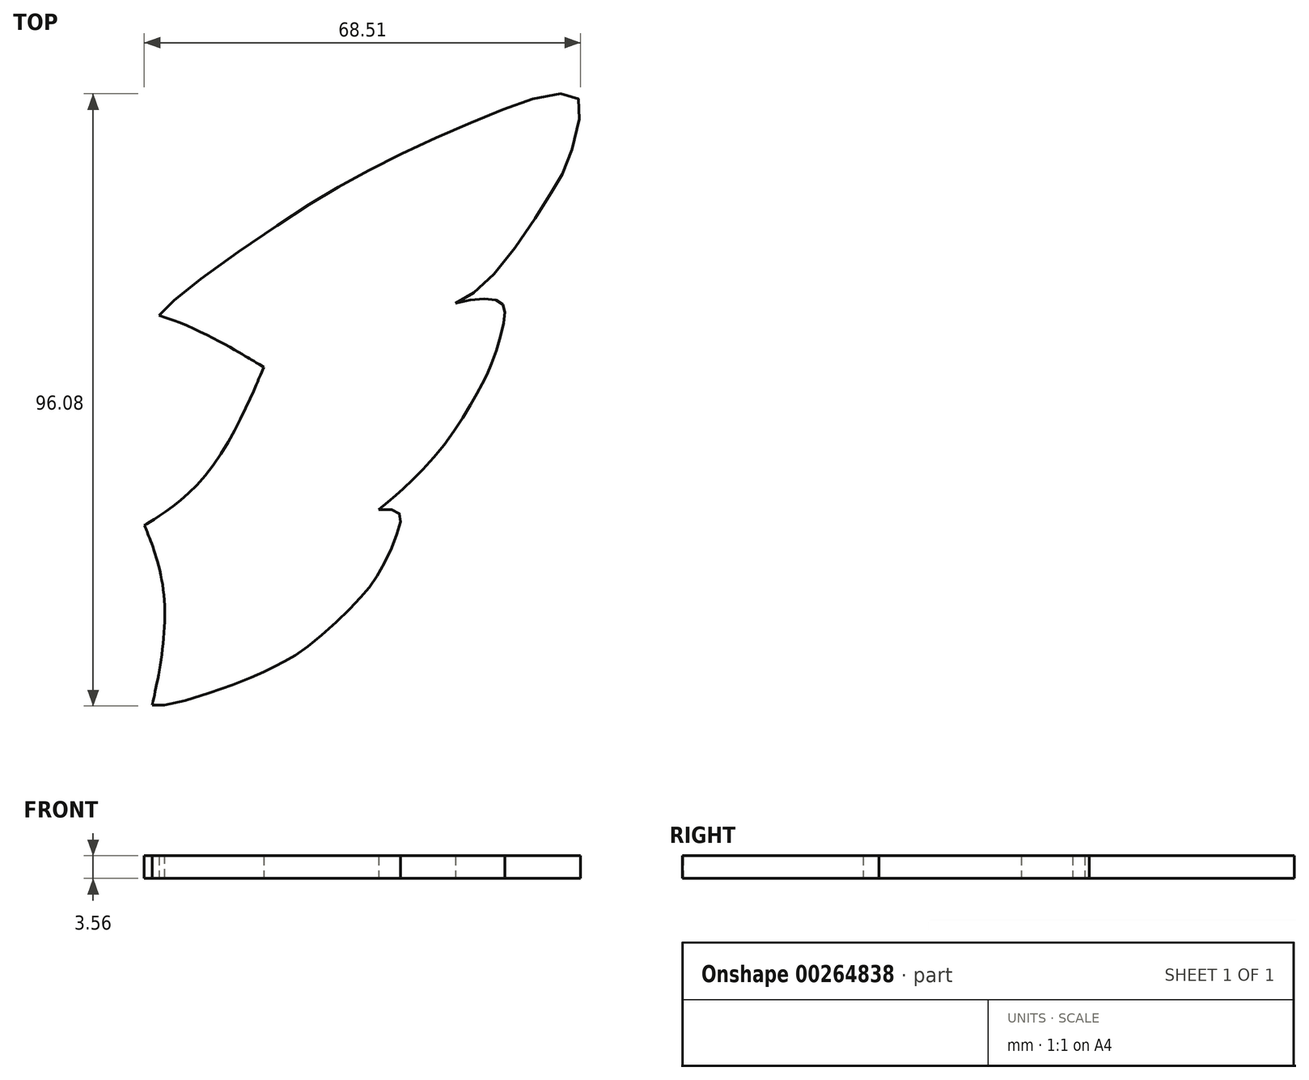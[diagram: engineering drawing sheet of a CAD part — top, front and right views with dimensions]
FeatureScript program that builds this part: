
annotation { "Feature Type Name" : "Feature", "Feature Type Description" : "" }
export const myFeature = defineFeature(function(context is Context, id is Id, definition is map)
    precondition{}
    {
        {
            var Q0;
            Q0=qCreatedBy(makeId("Top.planeOp"),FACE);
            var sketch = newSketch(context, id + "F0", { "sketchPlane" : qUnion([Q0])});
            skFitSpline(sketch, "E0", {"points": [v(0, 50.02) * mm, v(-2.2, 48.08) * mm, v(-12.76, 36.88) * mm, v(-17.4, 26.21) * mm, v(-17.8, 24.5) * mm], "startDerivative": vector(-30.31, -26.69) * mm, "endDerivative": vector(-1.54, -10.44) * mm});
            skFitSpline(sketch, "E1.MirrorCS", {"points": [v(0, 50.02) * mm, v(2.2, 48.08) * mm, v(12.8, 36.85) * mm, v(17.4, 26.21) * mm, v(17.8, 24.5) * mm], "startDerivative": vector(30.31, -26.69) * mm, "endDerivative": vector(1.54, -10.44) * mm});
            skFitSpline(sketch, "E2.MirrorCS", {"points": [v(-47.57, 15.46) * mm, v(-46.4, 12.77) * mm, v(-39, -0.79) * mm, v(-30.3, -8.44) * mm, v(-28.8, -9.36) * mm], "startDerivative": vector(16.01, -37.08) * mm, "endDerivative": vector(9.45, -4.7) * mm});
            skFitSpline(sketch, "E3.MirrorCS", {"points": [v(-29.4, -40.48) * mm, v(-30.02, -37.6) * mm, v(-32.02, -22.29) * mm, v(-29.48, -10.98) * mm, v(-28.8, -9.35) * mm], "startDerivative": vector(-8.84, 39.4) * mm, "endDerivative": vector(4.89, 9.35) * mm});
            skFitSpline(sketch, "E4.MirrorCS", {"points": [v(-29.4, -40.47) * mm, v(-26.49, -40.19) * mm, v(-11.3, -37.34) * mm, v(-1.34, -31.43) * mm, v(0, -30.27) * mm], "startDerivative": vector(40.21, 3.77) * mm, "endDerivative": vector(7.38, 7.54) * mm});
            skFitSpline(sketch, "E5.MirrorCS", {"points": [v(47.57, 15.46) * mm, v(45.05, 16.95) * mm, v(31.1, 23.56) * mm, v(19.56, 24.64) * mm, v(17.8, 24.5) * mm], "startDerivative": vector(-34.75, 20.58) * mm, "endDerivative": vector(-10.4, -1.76) * mm});
            skFitSpline(sketch, "E6.MirrorCS", {"points": [v(47.57, 15.46) * mm, v(46.4, 12.77) * mm, v(39, -0.79) * mm, v(30.3, -8.44) * mm, v(28.8, -9.35) * mm], "startDerivative": vector(-16.01, -37.08) * mm, "endDerivative": vector(-9.45, -4.7) * mm});
            skFitSpline(sketch, "E7.MirrorCS", {"points": [v(29.4, -40.47) * mm, v(30.04, -37.61) * mm, v(32.02, -22.29) * mm, v(29.48, -10.98) * mm, v(28.8, -9.35) * mm], "startDerivative": vector(8.84, 39.4) * mm, "endDerivative": vector(-4.89, 9.35) * mm});
            skFitSpline(sketch, "E8.MirrorCS", {"points": [v(29.4, -40.47) * mm, v(26.49, -40.19) * mm, v(11.3, -37.34) * mm, v(1.34, -31.43) * mm, v(0, -30.27) * mm], "startDerivative": vector(-40.21, 3.77) * mm, "endDerivative": vector(-7.38, 7.54) * mm});
            skFitSpline(sketch, "E9", {"points": [v(-44.74, 9.03) * mm, v(-47.83, 11.93) * mm, v(-58.76, 17.58) * mm, v(-71.1, 22.52) * mm, v(-77.7, 25.45) * mm, v(-84.54, 25.78) * mm, v(-85.35, 23.17) * mm, v(-83.22, 15.7) * mm, v(-80.9, 11.09) * mm, v(-75.57, 2.87) * mm, v(-69.32, -3.73) * mm, v(-65.57, -6.92) * mm], "startDerivative": vector(-43.43, 53.76) * mm, "endDerivative": vector(69.28, -56.08) * mm});
            skFitSpline(sketch, "E10", {"points": [v(-31.96, -21.18) * mm, v(-44.8, -14.39) * mm, v(-54.86, -10.25) * mm, v(-63.69, -7.24) * mm, v(-68.7, -7.32) * mm, v(-68.73, -9.96) * mm, v(-65.64, -16.86) * mm, v(-61.83, -21.7) * mm, v(-53.89, -28.82) * mm, v(-49.47, -31.42) * mm, v(-43.27, -34.16) * mm, v(-30.02, -37.6) * mm], "startDerivative": vector(9.5, 5.9) * mm, "endDerivative": vector(32.53, 17.83) * mm});
            skLineSegment(sketch, "E11", {"start": v(0, 0) * mm, "end": v(-18.5, 25.45) * mm, "construction": true});
            skFitSpline(sketch, "E12.MirrorCS", {"points": [v(31.13, 23.54) * mm, v(34.77, 27.05) * mm, v(49.75, 37.71) * mm, v(59.9, 44.07) * mm, v(70.83, 49.72) * mm, v(82.9, 55) * mm, v(91.6, 58) * mm, v(96.6, 57.9) * mm, v(97.21, 55) * mm, v(95.02, 46.93) * mm, v(92.97, 43.22) * mm, v(87.64, 35) * mm, v(81.38, 27.8) * mm, v(77.7, 25.45) * mm], "startDerivative": vector(45.91, 50.59) * mm, "endDerivative": vector(-63.53, -33.64) * mm});
            skFitSpline(sketch, "E13.MirrorCS", {"points": [v(44.74, 9.03) * mm, v(47.83, 11.93) * mm, v(58.76, 17.58) * mm, v(71.1, 22.52) * mm, v(77.7, 25.45) * mm, v(84.54, 25.78) * mm, v(85.35, 23.17) * mm, v(83.22, 15.7) * mm, v(80.9, 11.09) * mm, v(75.57, 2.87) * mm, v(69.32, -3.73) * mm, v(65.57, -6.92) * mm], "startDerivative": vector(43.43, 53.76) * mm, "endDerivative": vector(-69.28, -56.08) * mm});
            skFitSpline(sketch, "E14.MirrorCS", {"points": [v(31.96, -21.18) * mm, v(44.8, -14.39) * mm, v(54.86, -10.25) * mm, v(63.69, -7.24) * mm, v(68.7, -7.32) * mm, v(68.73, -9.96) * mm, v(65.64, -16.86) * mm, v(61.83, -21.7) * mm, v(53.89, -28.82) * mm, v(49.47, -31.42) * mm, v(43.27, -34.16) * mm, v(30.02, -37.6) * mm], "startDerivative": vector(-9.5, 5.9) * mm, "endDerivative": vector(-32.53, 17.83) * mm});
            skFitSpline(sketch, "E15.MirrorCS", {"points": [v(31.13, 23.54) * mm, v(34.77, 27.05) * mm, v(49.75, 37.71) * mm, v(59.9, 44.07) * mm, v(70.83, 49.72) * mm, v(82.9, 55) * mm, v(91.6, 58) * mm, v(96.6, 57.9) * mm, v(97.21, 55) * mm, v(95.02, 46.93) * mm, v(92.97, 43.22) * mm, v(87.64, 35) * mm, v(81.38, 27.8) * mm, v(77.7, 25.45) * mm], "startDerivative": vector(45.91, 50.59) * mm, "endDerivative": vector(-63.53, -33.64) * mm});
            skFitSpline(sketch, "E16.MirrorCS", {"points": [v(-47.57, 15.46) * mm, v(-45.05, 16.95) * mm, v(-31.1, 23.56) * mm, v(-19.56, 24.64) * mm, v(-17.8, 24.5) * mm], "startDerivative": vector(34.75, 20.58) * mm, "endDerivative": vector(10.4, -1.76) * mm});
            skFitSpline(sketch, "E17.MirrorCS", {"points": [v(-31.13, 23.54) * mm, v(-34.77, 27.05) * mm, v(-49.75, 37.71) * mm, v(-59.9, 44.07) * mm, v(-70.83, 49.72) * mm, v(-82.9, 55) * mm, v(-91.6, 58) * mm, v(-96.6, 57.9) * mm, v(-97.21, 55) * mm, v(-95.02, 46.93) * mm, v(-92.97, 43.22) * mm, v(-87.64, 35) * mm, v(-81.38, 27.8) * mm, v(-77.7, 25.45) * mm], "startDerivative": vector(-45.91, 50.59) * mm, "endDerivative": vector(63.53, -33.64) * mm});
            skSolve(sketch);
        }
        {
            var Q0;
            {var subQ0=sQuery(id+"F0.wireOp",EDGE,"E6.MirrorCS");Q0=makeQuery(id+"F0.imprint","IMPRINT",FACE,{"disambiguationData":[TD([[makeQuery(id+"F0.imprint","IMPRINT",EDGE,{"derivedFrom":subQ0}),1.0]])]});}
            var Q1;
            {var subQ0=sQuery(id+"F0.wireOp",EDGE,"E14.MirrorCS");var subQ1=sQuery(id+"F0.wireOp",EDGE,"E7.MirrorCS");var subQ2=makeQuery(id+"F0.imprint","INTERSECT",VERTEX,{"disambiguationData":[OD(0.0)],"derivedFrom":[subQ1,subQ0]});Q1=makeQuery(id+"F0.imprint","IMPRINT",FACE,{"disambiguationData":[TD([[makeQuery(id+"F0.imprint","IMPRINT",EDGE,{"disambiguationData":[TD([[subQ2,-1.0]])],"derivedFrom":subQ1}),-1.0]])]});}
            extrude(context, id + "F1", {"entities" : qUnion([Q0, Q1]), "depth" : 3.56 * mm});
        }
    });
